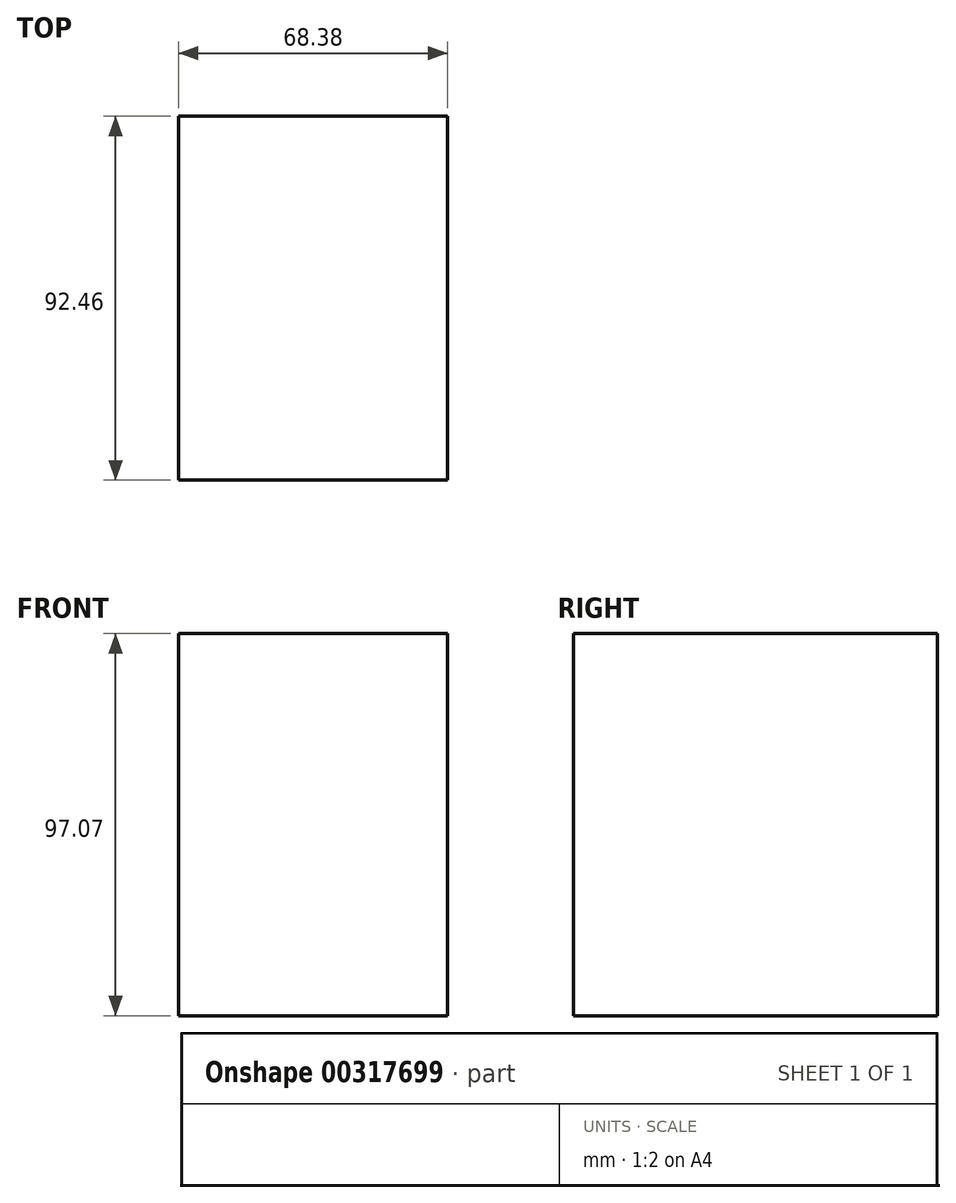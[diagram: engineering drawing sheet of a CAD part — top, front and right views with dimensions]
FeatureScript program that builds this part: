
annotation { "Feature Type Name" : "Feature", "Feature Type Description" : "" }
export const myFeature = defineFeature(function(context is Context, id is Id, definition is map)
    precondition{}
    {
        {
            var Q0;
            Q0=qCreatedBy(makeId("Top.planeOp"),FACE);
            var sketch = newSketch(context, id + "F0", { "sketchPlane" : qUnion([Q0])});
            skLineSegment(sketch, "E0.bottom", {"start": v(38.78, -27.57) * mm, "end": v(-29.6, -27.57) * mm});
            skLineSegment(sketch, "E0.top", {"start": v(38.78, 64.9) * mm, "end": v(-29.6, 64.9) * mm});
            skLineSegment(sketch, "E0.left", {"start": v(38.78, -27.57) * mm, "end": v(38.78, 64.9) * mm});
            skLineSegment(sketch, "E0.right", {"start": v(-29.6, -27.57) * mm, "end": v(-29.6, 64.9) * mm});
            skSolve(sketch);
        }
        {
            var Q0;
            Q0 = qSketchRegion(id + "F0", true);
            extrude(context, id + "F1", {"entities" : qUnion([Q0]), "depth" : 97.07 * mm});
        }
    });
